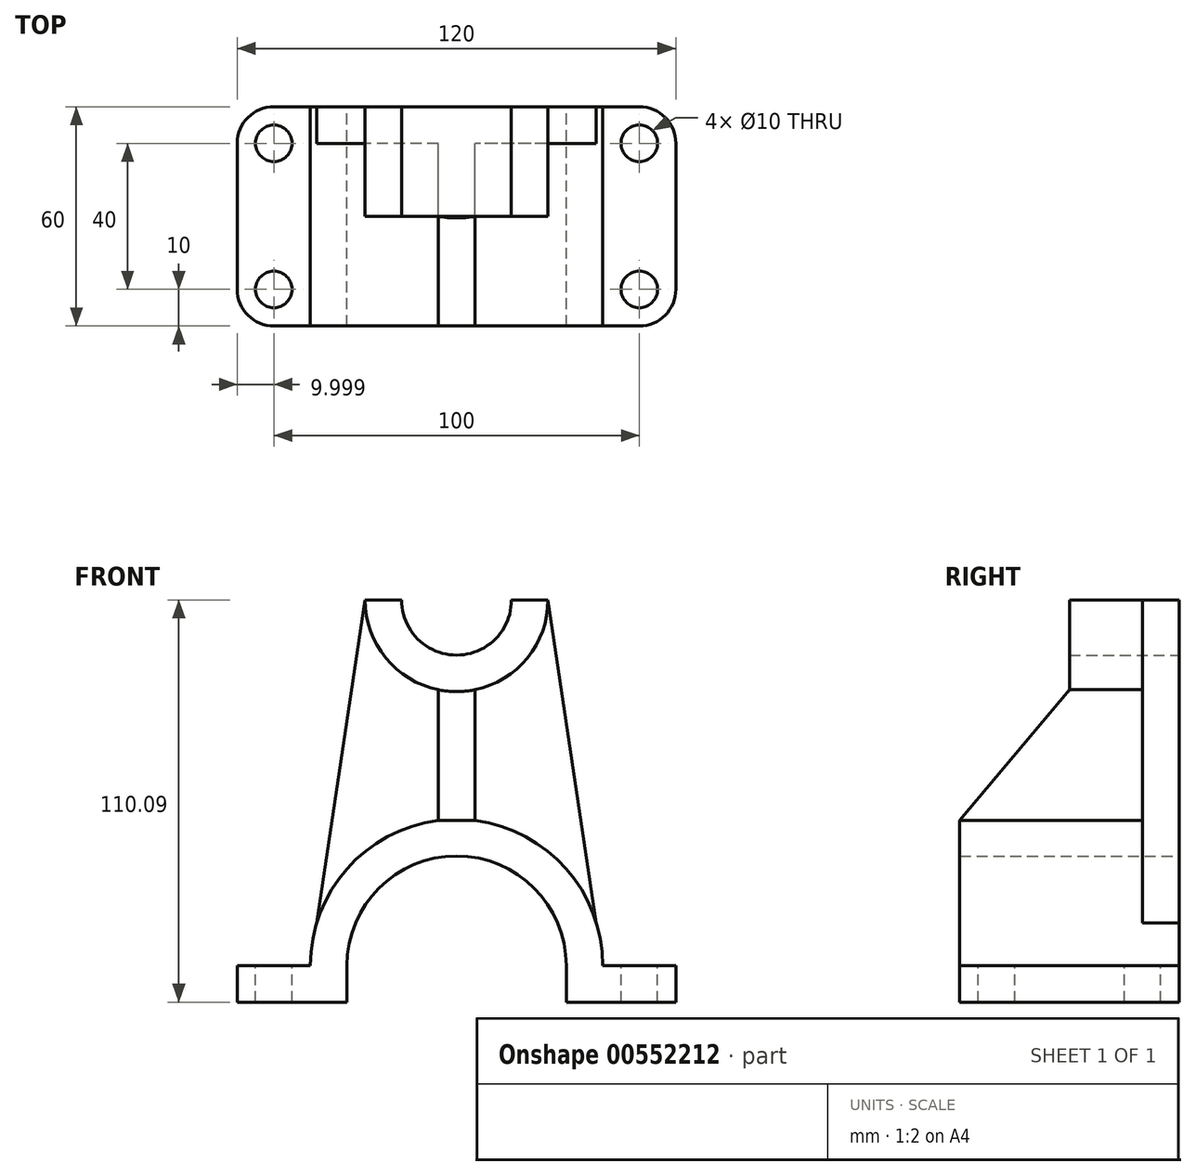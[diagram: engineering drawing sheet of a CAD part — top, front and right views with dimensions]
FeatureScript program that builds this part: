
annotation { "Feature Type Name" : "Feature", "Feature Type Description" : "" }
export const myFeature = defineFeature(function(context is Context, id is Id, definition is map)
    precondition{}
    {
        {
            var Q0;
            Q0=qCreatedBy(makeId("Front.planeOp"),FACE);
            var sketch = newSketch(context, id + "F0", { "sketchPlane" : qUnion([Q0])});
            skLineSegment(sketch, "E0.bottom", {"start": v(-54.38, -42.37) * mm, "end": v(-34.38, -42.37) * mm});
            skLineSegment(sketch, "E0.top", {"start": v(-54.38, -52.37) * mm, "end": v(-24.38, -52.37) * mm});
            skLineSegment(sketch, "E0.left", {"start": v(-54.38, -42.37) * mm, "end": v(-54.38, -52.37) * mm});
            skLineSegment(sketch, "E0.right", {"start": v(65.62, -42.37) * mm, "end": v(65.62, -52.37) * mm});
            skArc(sketch, "E1", {"start": v(35.62, -42.37) * mm, "mid": v(5.62, -12.37) * mm, "end": v(-24.38, -42.37) * mm});
            skArc(sketch, "E2", {"start": v(45.62, -42.37) * mm, "mid": v(5.62, -2.37) * mm, "end": v(-34.38, -42.37) * mm});
            skLineSegment(sketch, "E3.trimOffspring", {"start": v(45.62, -42.37) * mm, "end": v(65.62, -42.37) * mm});
            skLineSegment(sketch, "E4.trimOffspring", {"start": v(35.62, -52.37) * mm, "end": v(65.62, -52.37) * mm});
            skPoint(sketch, "E5.endSnap0", {"position": v(-38.52, -52.37) * mm});
            skLineSegment(sketch, "E6.0", {"start": v(-24.38, -42.37) * mm, "end": v(-24.38, -52.37) * mm});
            skLineSegment(sketch, "E7.0", {"start": v(35.62, -42.37) * mm, "end": v(35.62, -52.37) * mm});
            skPoint(sketch, "E8.orphan", {"position": v(-22.66, -52.37) * mm});
            skPoint(sketch, "E5.end.orphan", {"position": v(-24.38, -52.37) * mm});
            skSolve(sketch);
        }
        {
            var Q0;
            Q0=makeQuery(id+"F0.imprint","IMPRINT",FACE,{"disambiguationData":[TD([[makeQuery(id+"F0.imprint","IMPRINT",EDGE,{"derivedFrom":sQuery(id+"F0.wireOp",EDGE,"E0.bottom")}),-1.0]])]});
            extrude(context, id + "F1", {"entities" : qUnion([Q0]), "depth" : 60 * mm, "offsetDistance" : 25 * mm});
        }
        {
            var Q0;
            Q0=makeQuery(id+"F1.opExtrude","CAP_FACE",FACE,{"disambiguationData":[OSD([sQuery(id+"F0.wireOp",EDGE,"E0.bottom"),sQuery(id+"F0.wireOp",EDGE,"E0.top"),sQuery(id+"F0.wireOp",EDGE,"E0.left"),sQuery(id+"F0.wireOp",EDGE,"E0.right"),sQuery(id+"F0.wireOp",EDGE,"E1"),sQuery(id+"F0.wireOp",EDGE,"E2"),sQuery(id+"F0.wireOp",EDGE,"E3.trimOffspring"),sQuery(id+"F0.wireOp",EDGE,"E4.trimOffspring"),sQuery(id+"F0.wireOp",EDGE,"E6.0"),sQuery(id+"F0.wireOp",EDGE,"E7.0")])],"isStart":true});
            var sketch = newSketch(context, id + "F2", { "sketchPlane" : qUnion([Q0])});
            skArc(sketch, "E9", {"start": v(-20.62, 57.72) * mm, "mid": v(-5.62, 42.63) * mm, "end": v(9.38, 57.72) * mm});
            skPoint(sketch, "E9.centerSnap0", {"position": v(-5.62, -12.37) * mm});
            skArc(sketch, "E10", {"start": v(-30.62, 57.72) * mm, "mid": v(-5.62, 32.63) * mm, "end": v(19.38, 57.72) * mm});
            skLineSegment(sketch, "E11", {"start": v(-30.62, 57.72) * mm, "end": v(19.38, 57.72) * mm, "construction": true});
            skLineSegment(sketch, "E12", {"start": v(-30.62, 57.72) * mm, "end": v(-20.62, 57.72) * mm});
            skLineSegment(sketch, "E13", {"start": v(9.38, 57.72) * mm, "end": v(19.38, 57.72) * mm});
            skLineSegment(sketch, "E14", {"start": v(-30.62, 57.72) * mm, "end": v(-45.62, -42.37) * mm});
            skLineSegment(sketch, "E15", {"start": v(19.38, 57.72) * mm, "end": v(34.38, -42.37) * mm});
            skSolve(sketch);
        }
        {
            var Q0;
            {var subQ0=sQuery(id+"F2.wireOp",EDGE,"E10");Q0=makeQuery(id+"F2.imprint","IMPRINT",FACE,{"disambiguationData":[TD([[makeQuery(id+"F2.imprint","IMPRINT",EDGE,{"derivedFrom":subQ0}),-1.0]])]});}
            extrude(context, id + "F3", {"entities" : qUnion([Q0]), "operationType" : NewBodyOperationType.ADD, "oppositeDirection" : true, "depth" : 10 * mm, "offsetDistance" : 25 * mm});
        }
        {
            var Q0;
            Q0=makeQuery(id+"F2.imprint","IMPRINT",FACE,{"disambiguationData":[TD([[makeQuery(id+"F2.imprint","IMPRINT",EDGE,{"derivedFrom":sQuery(id+"F2.wireOp",EDGE,"E9")}),-1.0]])]});
            extrude(context, id + "F4", {"entities" : qUnion([Q0]), "operationType" : NewBodyOperationType.ADD, "oppositeDirection" : true, "depth" : 30 * mm, "offsetDistance" : 25 * mm});
        }
        {
            var Q0;
            Q0=makeQuery(id+"F3.opExtrude","CAP_FACE",FACE,{"disambiguationData":[OSD([sQuery(id+"F0.wireOp",EDGE,"E2"),sQuery(id+"F2.wireOp",EDGE,"E10"),sQuery(id+"F2.wireOp",EDGE,"E14"),sQuery(id+"F2.wireOp",EDGE,"E15")])],"isStart":false});
            var sketch = newSketch(context, id + "F5", { "sketchPlane" : qUnion([Q0])});
            skLineSegment(sketch, "E16", {"start": v(5.62, 32.63) * mm, "end": v(5.62, -2.37) * mm, "construction": true});
            skLineSegment(sketch, "E17", {"start": v(0.62, 33.14) * mm, "end": v(0.62, -2.68) * mm});
            skLineSegment(sketch, "E18", {"start": v(10.62, 33.14) * mm, "end": v(10.62, -2.68) * mm});
            skSolve(sketch);
        }
        {
            var Q0;
            {var subQ0=sQuery(id+"F5.wireOp",EDGE,"E17");Q0=makeQuery(id+"F5.imprint","IMPRINT",FACE,{"disambiguationData":[TD([[makeQuery(id+"F5.imprint","IMPRINT",EDGE,{"derivedFrom":subQ0}),1.0]])]});}
            var Q1;
            Q1=makeQuery(id+"F1.opExtrude","CAP_FACE",FACE,{"disambiguationData":[OSD([sQuery(id+"F0.wireOp",EDGE,"E0.bottom"),sQuery(id+"F0.wireOp",EDGE,"E0.top"),sQuery(id+"F0.wireOp",EDGE,"E0.left"),sQuery(id+"F0.wireOp",EDGE,"E0.right"),sQuery(id+"F0.wireOp",EDGE,"E1"),sQuery(id+"F0.wireOp",EDGE,"E2"),sQuery(id+"F0.wireOp",EDGE,"E3.trimOffspring"),sQuery(id+"F0.wireOp",EDGE,"E4.trimOffspring"),sQuery(id+"F0.wireOp",EDGE,"E6.0"),sQuery(id+"F0.wireOp",EDGE,"E7.0")])],"isStart":false});
            extrude(context, id + "F6", {"entities" : qUnion([Q0]), "operationType" : NewBodyOperationType.ADD, "endBound" : BoundingType.UP_TO_SURFACE, "depth" : 25 * mm, "endBoundEntityFace" : qUnion([Q1]), "offsetDistance" : 25 * mm});
        }
        {
            var Q0;
            Q0=makeQuery(id+"F6.opExtrude","SWEPT_FACE",FACE,{"disambiguationData":[OSD([sQuery(id+"F5.wireOp",EDGE,"E18")])]});
            var sketch = newSketch(context, id + "F7", { "sketchPlane" : qUnion([Q0])});
            skLineSegment(sketch, "E19", {"start": v(-30, 33.14) * mm, "end": v(-60, -2.68) * mm});
            skSolve(sketch);
        }
        {
            var Q0;
            Q0=makeQuery(id+"F7.imprint","IMPRINT",FACE,{"disambiguationData":[TD([[makeQuery(id+"F7.imprint","IMPRINT",EDGE,{"derivedFrom":sQuery(id+"F7.wireOp",EDGE,"E19")}),-1.0]])]});
            extrude(context, id + "F8", {"entities" : qUnion([Q0]), "operationType" : NewBodyOperationType.REMOVE, "oppositeDirection" : true, "depth" : 25 * mm, "offsetDistance" : 25 * mm});
        }
        {
            var Q0;
            Q0=makeQuery(id+"F1.opExtrude","SWEPT_FACE",FACE,{"disambiguationData":[OSD([sQuery(id+"F0.wireOp",EDGE,"E3.trimOffspring")])]});
            var sketch = newSketch(context, id + "F9", { "sketchPlane" : qUnion([Q0])});
            skCircle(sketch, "E20", {"center": v(55.62, -50) * mm, "radius": 5 * mm});
            skPoint(sketch, "E20.centerSnap0", {"position": v(55.62, -60) * mm});
            skCircle(sketch, "E21.0.1.0", {"center": v(55.62, -10) * mm, "radius": 5 * mm});
            skCircle(sketch, "E21.1.0.0", {"center": v(-44.38, -50) * mm, "radius": 5 * mm});
            skCircle(sketch, "E21.1.1.0", {"center": v(-44.38, -10) * mm, "radius": 5 * mm});
            skLineSegment(sketch, "E21.direction1", {"start": v(55.62, -50) * mm, "end": v(-44.38, -50) * mm, "construction": true});
            skLineSegment(sketch, "E21.direction2", {"start": v(55.62, -50) * mm, "end": v(55.62, -10) * mm, "construction": true});
            skSolve(sketch);
        }
        {
            var Q0;
            Q0 = qSketchRegion(id + "F9", true);
            extrude(context, id + "F10", {"entities" : qUnion([Q0]), "operationType" : NewBodyOperationType.REMOVE, "oppositeDirection" : true, "depth" : 25 * mm, "offsetDistance" : 25 * mm});
        }
        {
            var Q0;
            Q0=makeQuery(id+"F1.opExtrude","CAP_EDGE",EDGE,{"disambiguationData":[OSD([sQuery(id+"F0.wireOp",EDGE,"E0.right")])],"isStart":false});
            var Q1;
            Q1=makeQuery(id+"F1.opExtrude","CAP_EDGE",EDGE,{"disambiguationData":[OSD([sQuery(id+"F0.wireOp",EDGE,"E0.right")])],"isStart":true});
            var Q2;
            Q2=makeQuery(id+"F1.opExtrude","CAP_EDGE",EDGE,{"disambiguationData":[OSD([sQuery(id+"F0.wireOp",EDGE,"E0.left")])],"isStart":false});
            var Q3;
            Q3=makeQuery(id+"F1.opExtrude","CAP_EDGE",EDGE,{"disambiguationData":[OSD([sQuery(id+"F0.wireOp",EDGE,"E0.left")])],"isStart":true});
            fillet(context, id + "F11", {"entities" : qUnion([Q0, Q1, Q2, Q3]), "radius" : 10 * mm, "tangentPropagation" : true, "allowEdgeOverflow" : false});
        }
    });
